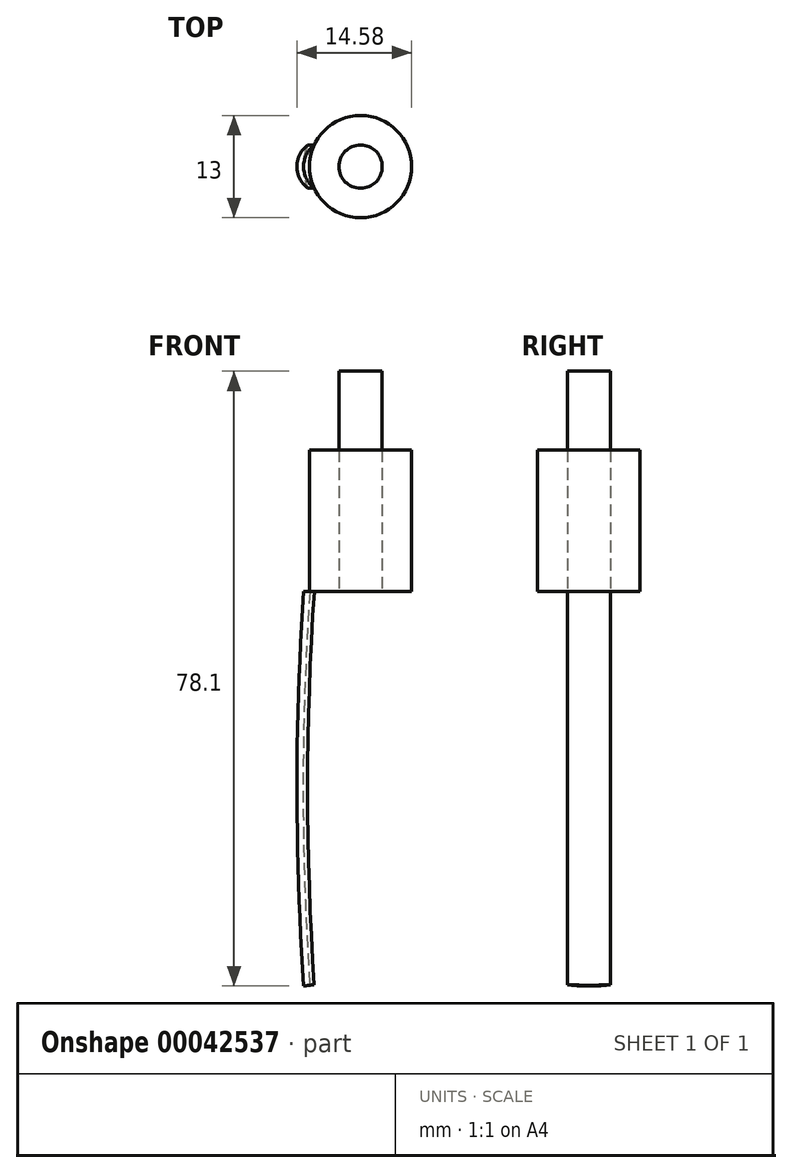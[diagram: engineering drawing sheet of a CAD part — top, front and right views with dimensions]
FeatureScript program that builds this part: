
annotation { "Feature Type Name" : "Feature", "Feature Type Description" : "" }
export const myFeature = defineFeature(function(context is Context, id is Id, definition is map)
    precondition{}
    {
        {
            var Q0;
            Q0=qCreatedBy(makeId("Top.planeOp"),FACE);
            var sketch = newSketch(context, id + "F0", { "sketchPlane" : qUnion([Q0])});
            skCircle(sketch, "E0", {"center": v(0, 0) * mm, "radius": 2.75 * mm});
            skSolve(sketch);
        }
        {
            var Q0;
            Q0=qCreatedBy(makeId("Top.planeOp"),FACE);
            var sketch = newSketch(context, id + "F1", { "sketchPlane" : qUnion([Q0])});
            skCircle(sketch, "E1", {"center": v(0, 0) * mm, "radius": 6.5 * mm});
            skSolve(sketch);
        }
        {
            var Q0;
            Q0=qCreatedBy(makeId("Top.planeOp"),FACE);
            var sketch = newSketch(context, id + "F2", { "sketchPlane" : qUnion([Q0])});
            skLineSegment(sketch, "E2", {"start": v(0, -2.75) * mm, "end": v(0, 2.75) * mm, "construction": true});
            skLineSegment(sketch, "E3", {"start": v(0, 2.75) * mm, "end": v(-5.89, 2.75) * mm, "construction": true});
            skLineSegment(sketch, "E4", {"start": v(0, -2.75) * mm, "end": v(-5.89, -2.75) * mm, "construction": true});
            skLineSegment(sketch, "E5", {"start": v(0, 0) * mm, "end": v(-6.5, 0) * mm, "construction": true});
            skSolve(sketch);
        }
        {
            var Q0;
            Q0=qCreatedBy(makeId("Top.planeOp"),FACE);
            var sketch = newSketch(context, id + "F3", { "sketchPlane" : qUnion([Q0])});
            skArc(sketch, "E6", {"start": v(-5.88, 2.73) * mm, "mid": v(-7.24, 0) * mm, "end": v(-5.88, -2.72) * mm});
            skArc(sketch, "E7", {"start": v(-5.88, 2.73) * mm, "mid": v(-6.45, 0) * mm, "end": v(-5.88, -2.72) * mm});
            skSolve(sketch);
        }
        {
            var Q0;
            Q0=qCreatedBy(makeId("Front.planeOp"),FACE);
            var sketch = newSketch(context, id + "F4", { "sketchPlane" : qUnion([Q0])});
            skLineSegment(sketch, "E8", {"start": v(-6.5, 0) * mm, "end": v(-6.5, -50) * mm});
            skArc(sketch, "E9", {"start": v(-6.5, 0) * mm, "mid": v(-7.34, -25) * mm, "end": v(-6.5, -50) * mm});
            skSolve(sketch);
        }
        {
            var Q0;
            Q0 = qSketchRegion(id + "F0", true);
            extrude(context, id + "F5", {"entities" : qUnion([Q0]), "depth" : 28 * mm});
        }
        {
            var Q0;
            Q0 = qSketchRegion(id + "F1", true);
            var Q1;
            Q1=sQuery(id+"F1.wireOp",EDGE,"E1");
            extrude(context, id + "F6", {"entities" : qUnion([Q0]), "surfaceEntities" : qUnion([Q1]), "depth" : 18 * mm});
        }
        {
            var Q0;
            Q0=makeQuery(id+"F3.imprint","IMPRINT",FACE,{"disambiguationData":[TD([[makeQuery(id+"F3.imprint","IMPRINT",EDGE,{"derivedFrom":sQuery(id+"F3.wireOp",EDGE,"E6")}),1.0]])]});
            var Q1;
            Q1=sQuery(id+"F3.wireOp",EDGE,"E6");
            var Q2;
            Q2=sQuery(id+"F3.wireOp",EDGE,"E7");
            var Q3;
            Q3=sQuery(id+"F4.wireOp",EDGE,"E9");
            sweep(context, id + "F7", {"profiles" : qUnion([Q0]), "surfaceProfiles" : qUnion([Q1, Q2]), "path" : qUnion([Q3])});
        }
    });
